# Revit family: Door_Overhead-Sectional-Panel_Haas_Carriage-Recessed-Long-74-73
name_source: partatom
category: Doors
units: mm (PartAtom-declared; Revit-internal decimal feet)

## family parameters
Always vertical = Yes
Classification Number = 23.30.10.17.37.14
Cut with Voids When Loaded = No
Room Calculation Point = No
Shared = No
Work Plane-Based = Yes

## types (2) — shared parameters
Assembly Code = B2030410
Default Elevation = 4' - 0"
Description = Haas Door Panel as Specified
Height = 8' - 0"
Keynote = 08360
Manufacturer = Haas Door Co.
Model = Haas Door Panel as Specified
Number Panels = 6
Thickness = 0' - 3"
URL = http://www.haasdoor.com
Width = 16' - 0"

## per-type parameters (varying)
| type | Section Type_Row 1 | Section Type_Row 10 | Section Type_Row 2 | Section Type_Row 3 | Section Type_Row 4 | Section Type_Row 5 | Section Type_Row 6 | Section Type_Row 7 | Section Type_Row 8 | Section Type_Row 9 |
| Carriage Default | HAAS_Section_Long-Carriage-74 : Carriage Design 74 | HAAS_Section_Long-Carriage-74 : Carriage Design 74 | HAAS_Section_Long-Carriage-74 : Carriage Design 74 | HAAS_Section_Long-Carriage-74 : Carriage Design 74 | HAAS_Section_Long-Carriage-74 : Carriage Design 74 Windowed as Specified | HAAS_Section_Long-Carriage-74 : Carriage Design 74 | HAAS_Section_Long-Carriage-74 : Carriage Design 74 | HAAS_Section_Long-Carriage-74 : Carriage Design 74 | HAAS_Section_Long-Carriage-74 : Carriage Design 74 | HAAS_Section_Long-Carriage-74 : Carriage Design 74 |
| Recessed Default | HAAS_Section_Long-Carriage-74 : Recessed Design 73 | HAAS_Section_Long-Carriage-74 : Recessed Design 73 | HAAS_Section_Long-Carriage-74 : Recessed Design 73 | HAAS_Section_Long-Carriage-74 : Recessed Design 73 | HAAS_Section_Long-Carriage-74 : Recessed Design 73 Windowed as Specified | HAAS_Section_Long-Carriage-74 : Recessed Design 73 | HAAS_Section_Long-Carriage-74 : Recessed Design 73 | HAAS_Section_Long-Carriage-74 : Recessed Design 73 | HAAS_Section_Long-Carriage-74 : Recessed Design 73 | HAAS_Section_Long-Carriage-74 : Recessed Design 73 |

## geometry (parser evidence)
native form markers: Sweep x5
no freeform markers — native parametric forms only
